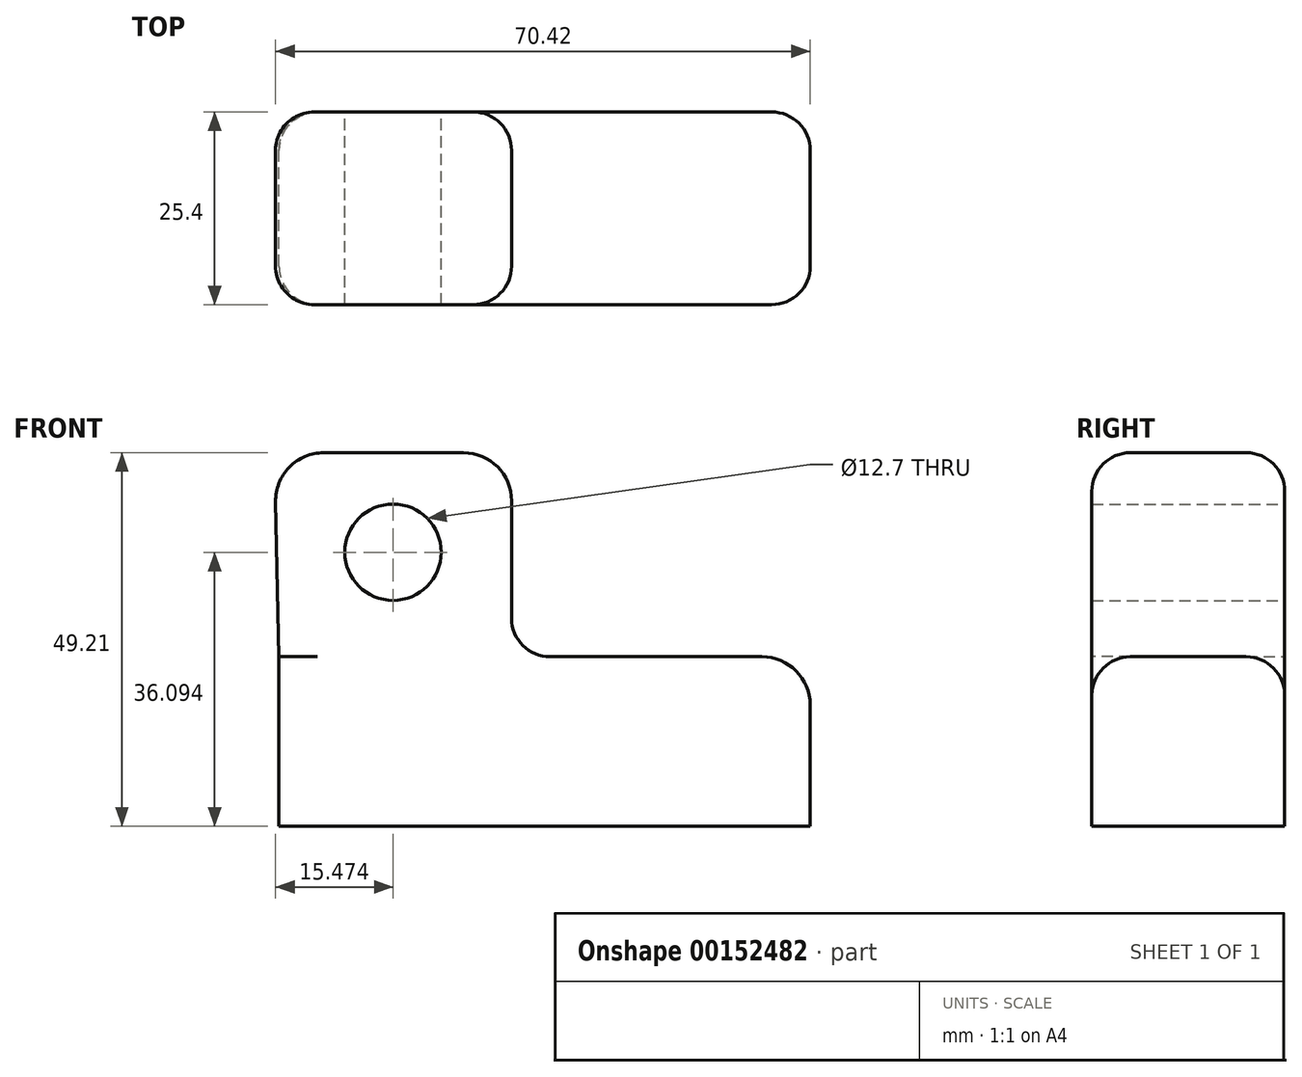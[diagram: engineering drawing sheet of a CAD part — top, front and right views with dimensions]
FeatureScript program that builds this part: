
annotation { "Feature Type Name" : "Feature", "Feature Type Description" : "" }
export const myFeature = defineFeature(function(context is Context, id is Id, definition is map)
    precondition{}
    {
        {
            var Q0;
            Q0=qCreatedBy(makeId("Front.planeOp"),FACE);
            var sketch = newSketch(context, id + "F0", { "sketchPlane" : qUnion([Q0])});
            skLineSegment(sketch, "E0", {"start": v(-30.64, 0) * mm, "end": v(-30.64, -22.32) * mm});
            skLineSegment(sketch, "E1", {"start": v(-30.64, -22.32) * mm, "end": v(39.33, -22.32) * mm});
            skLineSegment(sketch, "E2", {"start": v(39.33, -22.32) * mm, "end": v(39.33, -6.35) * mm});
            skLineSegment(sketch, "E3", {"start": v(32.98, 0) * mm, "end": v(0, 0) * mm});
            skLineSegment(sketch, "E4", {"start": v(0, 0) * mm, "end": v(0, 20.54) * mm});
            skLineSegment(sketch, "E5", {"start": v(-6.35, 26.89) * mm, "end": v(-24.74, 26.89) * mm});
            skLineSegment(sketch, "E6", {"start": v(-31.09, 20.4) * mm, "end": v(-30.64, 0) * mm});
            skCircle(sketch, "E7", {"center": v(-15.62, 13.77) * mm, "radius": 6.35 * mm});
            skPoint(sketch, "E8.visualSharp", {"position": v(39.33, 0) * mm});
            skArc(sketch, "E8.filletArc", {"start": v(39.33, -6.35) * mm, "mid": v(37.47, -1.86) * mm, "end": v(32.98, 0) * mm});
            skPoint(sketch, "E9.visualSharp", {"position": v(0, 26.89) * mm});
            skArc(sketch, "E9.filletArc", {"start": v(0, 20.54) * mm, "mid": v(-1.86, 25.03) * mm, "end": v(-6.35, 26.89) * mm});
            skPoint(sketch, "E10.visualSharp", {"position": v(-31.23, 26.89) * mm});
            skArc(sketch, "E10.filletArc", {"start": v(-24.74, 26.89) * mm, "mid": v(-29.28, 24.98) * mm, "end": v(-31.09, 20.4) * mm});
            skSolve(sketch);
        }
        {
            var Q0;
            Q0 = qSketchRegion(id + "F0", true);
            extrude(context, id + "F1", {"entities" : qUnion([Q0]), "endBound" : BoundingType.SYMMETRIC, "depth" : 25.4 * mm});
        }
        {
            var Q0;
            Q0=makeQuery(id+"F1.opExtrude","SWEPT_EDGE",EDGE,{"disambiguationData":[OSD([sQuery(id+"F0.wireOp",EDGE,"E3"),sQuery(id+"F0.wireOp",EDGE,"E4")])]});
            fillet(context, id + "F2", {"entities" : qUnion([Q0]), "radius" : 5.08 * mm, "tangentPropagation" : true, "allowEdgeOverflow" : false});
        }
        {
            var Q0;
            Q0=makeQuery(id+"F1.opExtrude","CAP_EDGE",EDGE,{"disambiguationData":[OSD([sQuery(id+"F0.wireOp",EDGE,"E5")])],"isStart":false});
            var Q1;
            Q1=makeQuery(id+"F1.opExtrude","CAP_EDGE",EDGE,{"disambiguationData":[OSD([sQuery(id+"F0.wireOp",EDGE,"E9.filletArc")])],"isStart":false});
            var Q2;
            Q2=makeQuery(id+"F1.opExtrude","CAP_EDGE",EDGE,{"disambiguationData":[OSD([sQuery(id+"F0.wireOp",EDGE,"E4")])],"isStart":true});
            fillet(context, id + "F3", {"entities" : qUnion([Q0, Q1, Q2]), "radius" : 5.08 * mm, "tangentPropagation" : true, "allowEdgeOverflow" : false});
        }
    });
